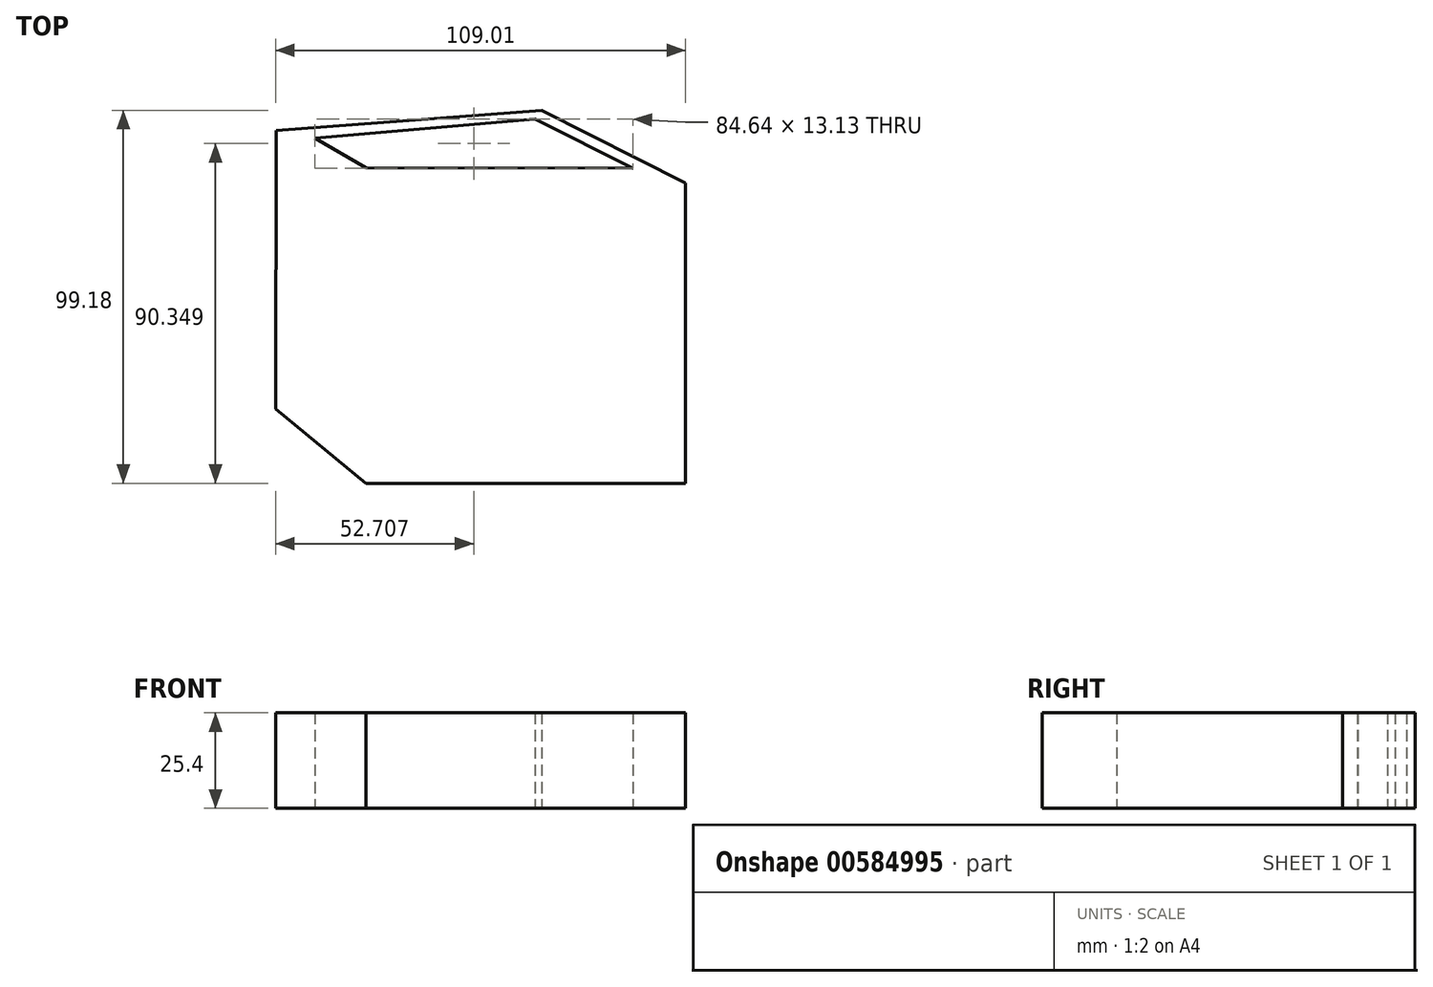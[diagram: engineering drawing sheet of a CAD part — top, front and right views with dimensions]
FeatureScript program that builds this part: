
annotation { "Feature Type Name" : "Feature", "Feature Type Description" : "" }
export const myFeature = defineFeature(function(context is Context, id is Id, definition is map)
    precondition{}
    {
        {
            var Q0;
            Q0=qCreatedBy(makeId("Top.planeOp"),FACE);
            var sketch = newSketch(context, id + "F0", { "sketchPlane" : qUnion([Q0])});
            skLineSegment(sketch, "E0", {"start": v(-46.76, 56.11) * mm, "end": v(-46.76, -24) * mm});
            skLineSegment(sketch, "E1", {"start": v(-46.76, -24) * mm, "end": v(38.26, -24) * mm});
            skLineSegment(sketch, "E2", {"start": v(38.26, -24) * mm, "end": v(38.26, 55.92) * mm});
            skLineSegment(sketch, "E3", {"start": v(38.26, 55.92) * mm, "end": v(-46.76, 56.11) * mm});
            skLineSegment(sketch, "E4", {"start": v(-4.63, 51.39) * mm, "end": v(-4.63, 56.02) * mm});
            skLineSegment(sketch, "E5", {"start": v(-4.63, 56.02) * mm, "end": v(-46.76, 56.11) * mm});
            skLineSegment(sketch, "E6", {"start": v(-46.76, -24) * mm, "end": v(-70.75, -4.16) * mm});
            skLineSegment(sketch, "E7", {"start": v(-70.75, -4.16) * mm, "end": v(-70.59, 69.9) * mm});
            skLineSegment(sketch, "E8", {"start": v(-70.59, 69.9) * mm, "end": v(-46.76, 56.11) * mm});
            skLineSegment(sketch, "E9", {"start": v(38.26, 55.92) * mm, "end": v(0, 75.2) * mm});
            skLineSegment(sketch, "E10", {"start": v(0, 75.2) * mm, "end": v(-70.59, 69.9) * mm});
            skLineSegment(sketch, "E11", {"start": v(-60.36, 67.82) * mm, "end": v(-46.76, 59.95) * mm});
            skLineSegment(sketch, "E12", {"start": v(-46.76, 59.95) * mm, "end": v(24.28, 59.8) * mm});
            skLineSegment(sketch, "E13", {"start": v(24.28, 59.8) * mm, "end": v(-1.8, 72.92) * mm});
            skLineSegment(sketch, "E14", {"start": v(-1.8, 72.92) * mm, "end": v(-60.36, 67.82) * mm});
            skSolve(sketch);
        }
        {
            var Q0;
            Q0 = qSketchRegion(id + "F0", true);
            extrude(context, id + "F1", {"entities" : qUnion([Q0]), "depth" : 25.4 * mm, "offsetDistance" : 25.4 * mm});
        }
    });
